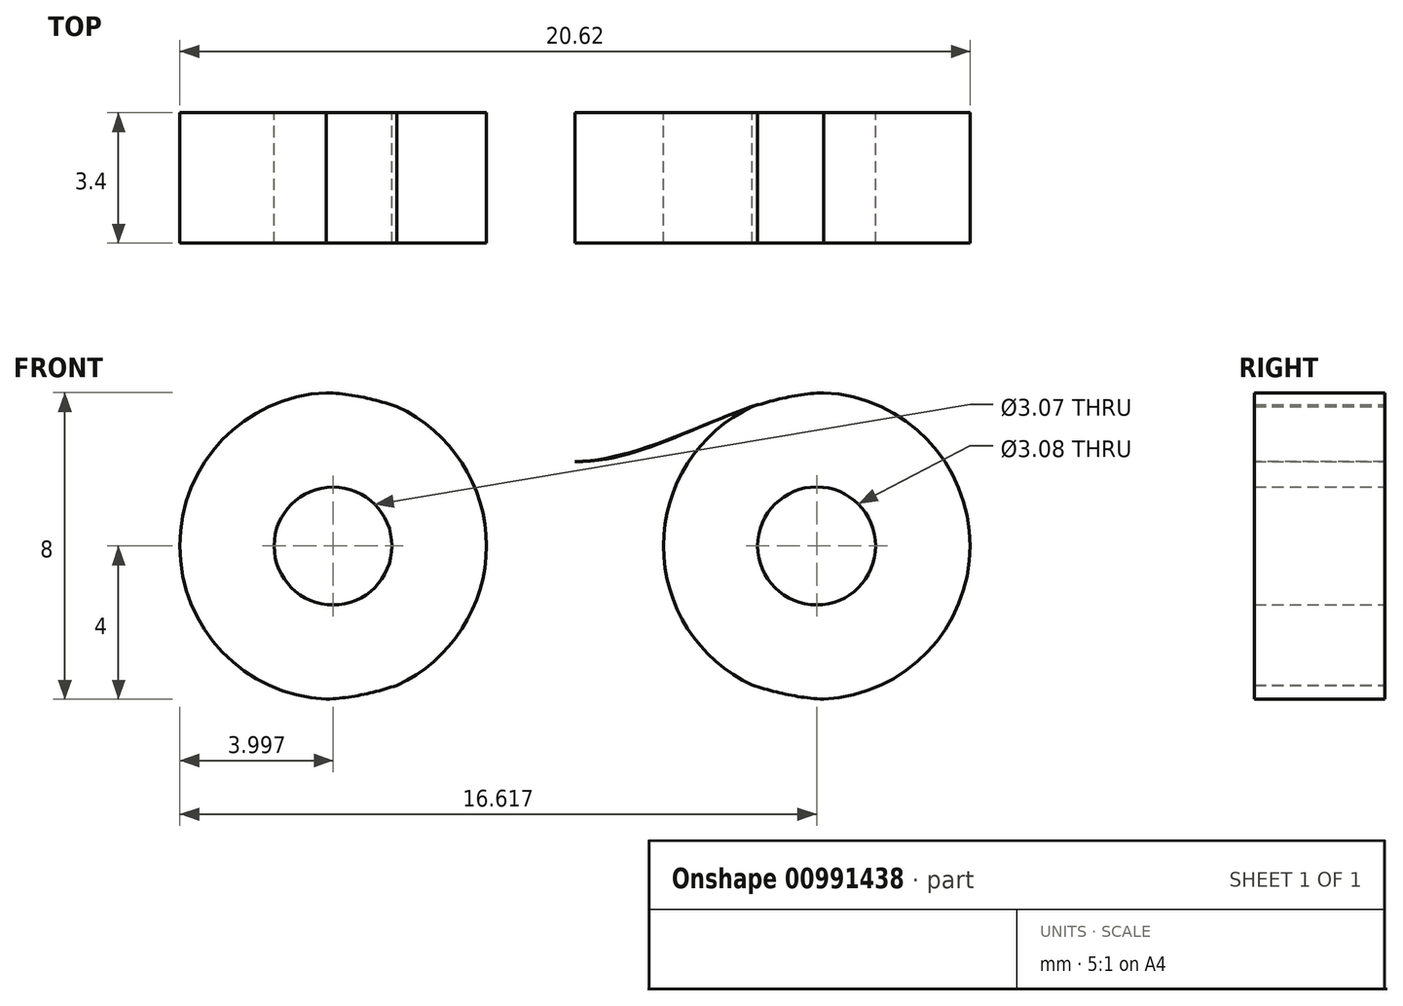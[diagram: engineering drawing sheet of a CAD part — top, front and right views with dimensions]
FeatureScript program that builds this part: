
annotation { "Feature Type Name" : "Feature", "Feature Type Description" : "" }
export const myFeature = defineFeature(function(context is Context, id is Id, definition is map)
    precondition{}
    {
        {
            var Q0;
            Q0=qCreatedBy(makeId("Front.planeOp"),FACE);
            var sketch = newSketch(context, id + "F0", { "sketchPlane" : qUnion([Q0])});
            skCircle(sketch, "E0", {"center": v(-6.31, 0) * mm, "radius": 1.54 * mm});
            skCircle(sketch, "E1", {"center": v(6.3, 0) * mm, "radius": 1.54 * mm});
            skCircle(sketch, "E2", {"center": v(6.3, 0) * mm, "radius": 4 * mm});
            skCircle(sketch, "E3", {"center": v(-6.31, 0) * mm, "radius": 4 * mm});
            skFitSpline(sketch, "E4", {"points": [v(-6.49, 4) * mm, v(0, 2.2) * mm, v(6.3, 4) * mm], "startDerivative": vector(14.5, -0.58) * mm, "endDerivative": vector(10.86, 0.01) * mm});
            skFitSpline(sketch, "E5.MirrorCS", {"points": [v(6.49, 4) * mm, v(0, 2.2) * mm, v(-6.3, 4) * mm], "startDerivative": vector(-14.5, -0.58) * mm, "endDerivative": vector(-10.86, 0.01) * mm});
            skFitSpline(sketch, "E6.MirrorCS", {"points": [v(-6.49, -4) * mm, v(0, -2.2) * mm, v(6.3, -4) * mm], "startDerivative": vector(14.5, 0.58) * mm, "endDerivative": vector(10.86, -0.01) * mm});
            skFitSpline(sketch, "E7.MirrorCS", {"points": [v(6.49, -4) * mm, v(0, -2.2) * mm, v(-6.3, -4) * mm], "startDerivative": vector(-14.5, 0.58) * mm, "endDerivative": vector(-10.86, -0.01) * mm});
            skSolve(sketch);
        }
        {
            var Q0;
            Q0=makeQuery(id+"F0.imprint","IMPRINT",FACE,{"disambiguationData":[TD([[makeQuery(id+"F0.imprint","IMPRINT",EDGE,{"derivedFrom":sQuery(id+"F0.wireOp",EDGE,"E0")}),-1.0]])]});
            var Q1;
            {var subQ1=sQuery(id+"F0.wireOp",EDGE,"E4");var subQ5=sQuery(id+"F0.wireOp",EDGE,"E2");var subQ6=makeQuery(id+"F0.imprint","INTERSECT",VERTEX,{"disambiguationData":[OD(1.0)],"derivedFrom":[subQ5,subQ1]});Q1=makeQuery(id+"F0.imprint","IMPRINT",FACE,{"disambiguationData":[TD([[makeQuery(id+"F0.imprint","IMPRINT",EDGE,{"disambiguationData":[TD([[subQ6,-1.0]])],"derivedFrom":subQ5}),-1.0]])]});}
            var Q2;
            Q2=makeQuery(id+"F0.imprint","IMPRINT",FACE,{"disambiguationData":[TD([[makeQuery(id+"F0.imprint","IMPRINT",EDGE,{"derivedFrom":sQuery(id+"F0.wireOp",EDGE,"E1")}),-1.0]])]});
            extrude(context, id + "F1", {"entities" : qUnion([Q0, Q1, Q2]), "depth" : 3.4 * mm, "offsetDistance" : 25.4 * mm});
        }
    });
